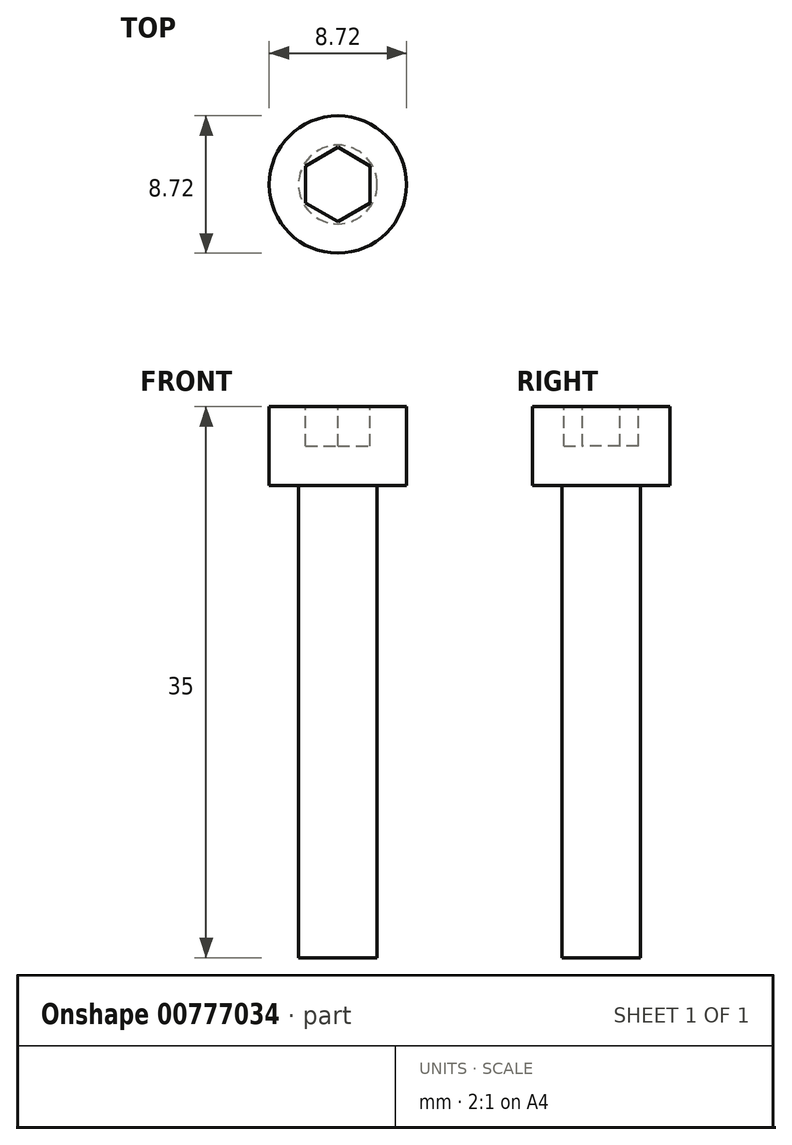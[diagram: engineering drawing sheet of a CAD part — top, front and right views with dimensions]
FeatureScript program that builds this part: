
annotation { "Feature Type Name" : "Feature", "Feature Type Description" : "" }
export const myFeature = defineFeature(function(context is Context, id is Id, definition is map)
    precondition{}
    {
        {
            var Q0;
            Q0=qCreatedBy(makeId("Top.planeOp"),FACE);
            var sketch = newSketch(context, id + "F0", { "sketchPlane" : qUnion([Q0])});
            skCircle(sketch, "E0", {"center": v(0, 0) * mm, "radius": 2.5 * mm});
            skSolve(sketch);
        }
        {
            var Q0;
            Q0=qSketchRegion(id+"F0",true);
            extrude(context, id + "F1", {"entities" : qUnion([Q0]), "depth" : 30 * mm, "offsetDistance" : 25 * mm});
        }
        {
            var Q0;
            Q0=makeQuery(id+"F1.opExtrude","CAP_FACE",FACE,{"disambiguationData":[OSD([sQuery(id+"F0.wireOp",EDGE,"E0")])],"isStart":false});
            var sketch = newSketch(context, id + "F2", { "sketchPlane" : qUnion([Q0])});
            skPoint(sketch, "E1", {"position": v(0, 0) * mm});
            skCircle(sketch, "E2", {"center": v(0, 0) * mm, "radius": 4.36 * mm});
            skSolve(sketch);
        }
        {
            var Q0;
            Q0=qSketchRegion(id+"F2",true);
            extrude(context, id + "F3", {"entities" : qUnion([Q0]), "operationType" : NewBodyOperationType.ADD, "depth" : 5 * mm, "offsetDistance" : 25 * mm});
        }
        {
            var Q0;
            Q0=makeQuery(id+"F3.opExtrude","CAP_FACE",FACE,{"disambiguationData":[OSD([sQuery(id+"F2.wireOp",EDGE,"E2")])],"isStart":false});
            var sketch = newSketch(context, id + "F4", { "sketchPlane" : qUnion([Q0])});
            skPoint(sketch, "E3", {"position": v(0, 0) * mm});
            skCircle(sketch, "E4.cCircle", {"center": v(0, 0) * mm, "radius": 2.05 * mm, "construction": true});
            skLineSegment(sketch, "E4.0", {"start": v(2.05, 1.18) * mm, "end": v(2.05, -1.18) * mm});
            skLineSegment(sketch, "E4.1", {"start": v(2.05, -1.18) * mm, "end": v(0, -2.36) * mm});
            skLineSegment(sketch, "E4.2", {"start": v(0, -2.36) * mm, "end": v(-2.05, -1.18) * mm});
            skLineSegment(sketch, "E4.3", {"start": v(-2.05, -1.18) * mm, "end": v(-2.05, 1.18) * mm});
            skLineSegment(sketch, "E4.4", {"start": v(-2.05, 1.18) * mm, "end": v(0, 2.36) * mm});
            skLineSegment(sketch, "E4.5", {"start": v(0, 2.36) * mm, "end": v(2.05, 1.18) * mm});
            skPoint(sketch, "E4.0.midPoint", {"position": v(2.05, 0) * mm});
            skSolve(sketch);
        }
        {
            var Q0;
            Q0=qSketchRegion(id+"F4",true);
            extrude(context, id + "F5", {"entities" : qUnion([Q0]), "operationType" : NewBodyOperationType.REMOVE, "oppositeDirection" : true, "depth" : 2.5 * mm, "offsetDistance" : 25 * mm});
        }
    });
